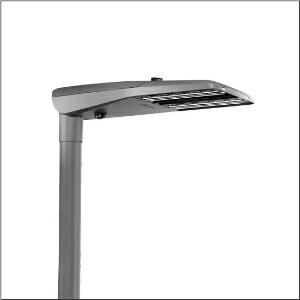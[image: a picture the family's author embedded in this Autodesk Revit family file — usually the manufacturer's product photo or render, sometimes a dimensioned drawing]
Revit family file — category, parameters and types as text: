
# Revit family: streetlight_sl_11_iq_midi___pc-l_5xc3e21y08me_ec69
name_source: partatom
category: Lighting Fixtures
units: mm (PartAtom-declared; Revit-internal decimal feet)

## family parameters
Cut with Voids When Loaded = No
Host = Face
Light Source = No
Part Type = Normal
Room Calculation Point = No
Round Connector Dimension = Use Diameter
Shared = No

## types (1)
- --- (1 x LED, 12730 lm, 122.8 W, 2200K)
    Apparent Load = 123 VA
    CIE Flux Codes = 37 73 96 100 100
    Color Rendering = 70
    Color Temperature = 2200K
    Default Elevation = 1800 mm
    Description = Streetlight SL 11 iQ midi, mast luminaire, primary light control with 3 zone facetted reflector, of plastic, silver coated, highly specular, primary optical cover: cover, of PMMA, transparent, light distribution: PC-L, light emission: direct distribution, primary light characteristic: asymmetric, left, installation type: post-top, side-entry, LED, High Power LED, rated luminous flux: 12.730lm, luminous efficacy: 104lm/W, light colour: 722, colour temperature: 2200K, control: presetting dimming logarithmic, Street-Remote, Auto-Match, Temp-Guard, Lumen-Switch, Night-Set, Smart-Wire, Light-Fading, Desk-Remote (wireless, voltage-free reading and setting of iQ features in the workshop via application-optimized NFC function/RFID function), optimised constant luminous flux control (CLO 2.0), with cable H07RN-F 5x 1.5mm², mains connection: 230..240V, AC, 50/60Hz, connection cable pre-assembled, cable length: 12,5m, start of lifetime: 123W, end of service life: 130W, reduction: 56W, luminaire housing, of diecast aluminium, powder-coated, Siteco® metallic grey (DB 702S), please order mast flange separately, inclination adjustable without tools: 0°, 5°, 10°, 15° (post-top) | 0°, -5°, -10°, -15° (side-entry), sealing non-destructively replaceable, multi-level sealing system, length: 780mm, width: 376mm, height: 118mm, mast flange for spigot size: 42mm (side-entry): 5XC10008XM4, 60/48mm (side-entry/post-top): 5XC10108XM2, 76/60mm (side-entry/post-top): 5XC10108XM1, equipment: Power, Smart Interface below and above, protection rating (complete): IP66, insulation class (complete): insulation class II (safety insulation), certification: CE, ENEC, VDE, UKCA, impact resistance: IK09, permissible operating ambient temperature for outdoor applications: -25..+50°C, standard-compliant lighting for roads and squares, Environmental Product Declaration (EPD) tested and certified by an independent institute, packaging unit: 1 piece

Light Distribution: PC-L
    Height = 118 mm
    Lamp = 1 x LED
    Lamp Light Flux = 12730 lm
    Lamp Power = 122.8 W
    Lamp count = 1
    Length = 780 mm
    Luminous efficacy = 104 lm/W
    Manufacturer = Siteco
    ModVariant = No
    Model = 5XC3E21Y08ME
    Number of Poles = 1
    OnlyDefault = Yes
    Power Factor = 1
    Product Name = Streetlight SL 11 iQ midi | PC-L
    Product group = mast luminaire | pylon top
    ProductGroupID = 6100
    Protection Class = Protection class II
    Protection Degree = IP 66
    RLX_Detail_Level = 1
    RLX_Emergency_Light_Flux = 0 lm
    RLX_Emergency_Type = 0
    RLX_Emergency_Type_DB = No
    RlxData = <blob elided: 73565 chars, md5=5bd74c0d>
    Socket = socket
    Standby Power = 0 W
    System Light Flux = 12729 lm
    System Power = 123 W
    Type Comments = factory setting: luminous flux: 100 % | dim-lin: 254 | 553 mA
    Type Image = l_1004429.jpg
    URL = http://relux.com
    VarID = @adj_076381
    Voltage = 0 V
    Weight = 0.00 kg
    Width = 376 mm

## geometry (parser evidence)
native form markers: Blend x4, Sweep x11
no freeform markers — native parametric forms only
